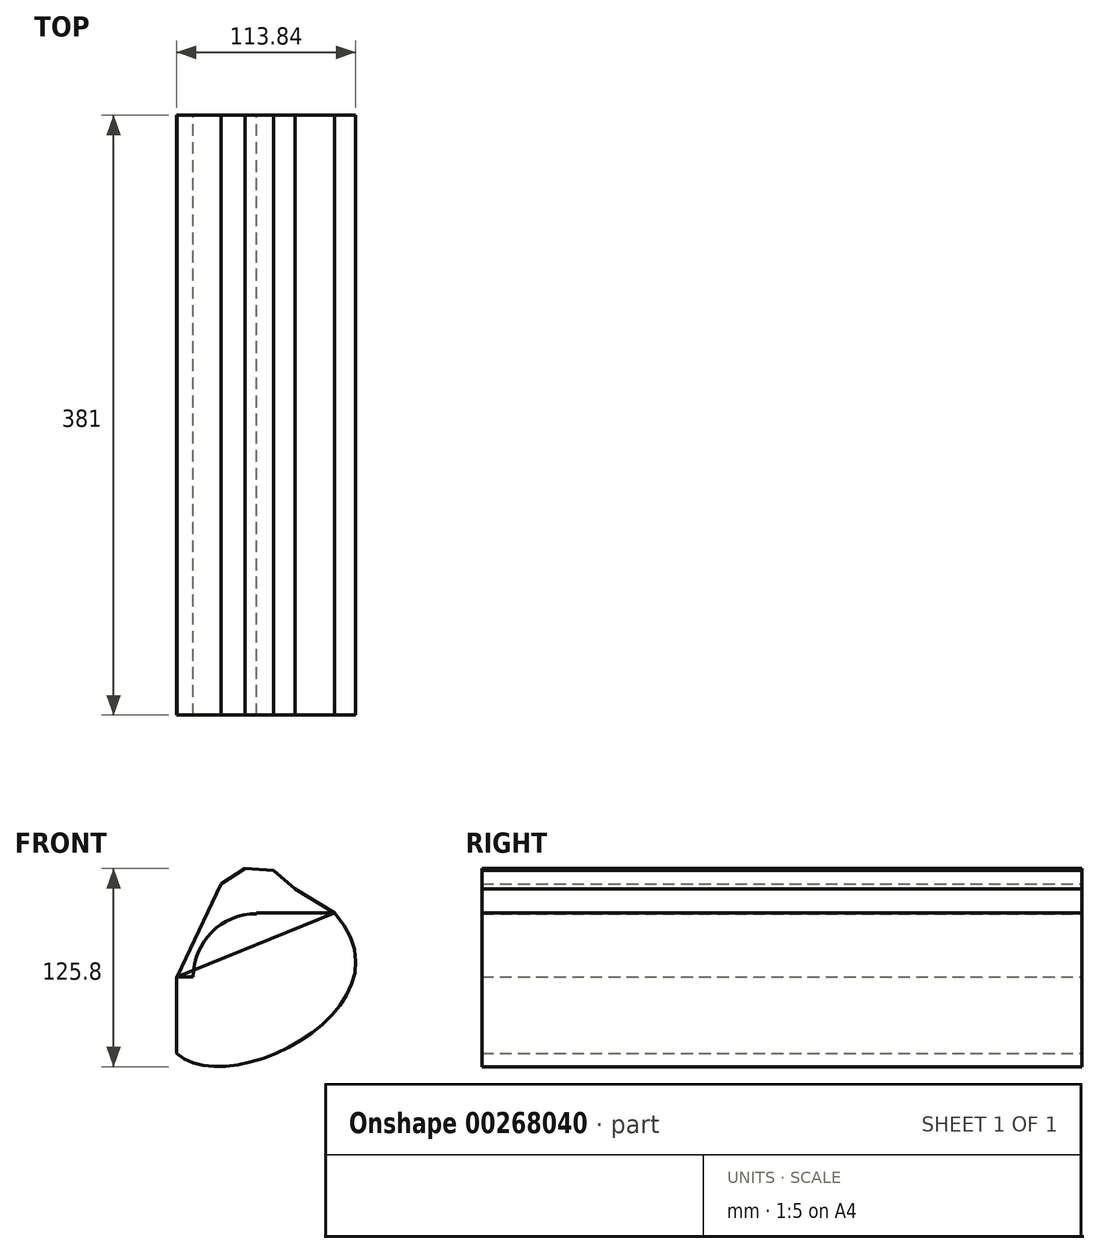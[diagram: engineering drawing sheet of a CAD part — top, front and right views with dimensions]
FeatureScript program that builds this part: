
annotation { "Feature Type Name" : "Feature", "Feature Type Description" : "" }
export const myFeature = defineFeature(function(context is Context, id is Id, definition is map)
    precondition{}
    {
        {
            var Q0;
            Q0=qCreatedBy(makeId("Front.planeOp"),FACE);
            var sketch = newSketch(context, id + "F0", { "sketchPlane" : qUnion([Q0])});
            skLineSegment(sketch, "E0.bottom", {"start": v(0, 0) * mm, "end": v(49.77, 0) * mm});
            skLineSegment(sketch, "E0.top", {"start": v(0, 40.47) * mm, "end": v(49.77, 40.47) * mm});
            skLineSegment(sketch, "E0.left", {"start": v(0, 0) * mm, "end": v(0, 40.47) * mm});
            skLineSegment(sketch, "E0.right", {"start": v(49.77, 0) * mm, "end": v(49.77, 40.47) * mm});
            skLineSegment(sketch, "E1.bottom", {"start": v(0, 0) * mm, "end": v(-50.7, 0) * mm});
            skLineSegment(sketch, "E1.top", {"start": v(0, -48.61) * mm, "end": v(-50.7, -48.61) * mm});
            skLineSegment(sketch, "E1.left", {"start": v(0, 0) * mm, "end": v(0, -48.61) * mm});
            skLineSegment(sketch, "E1.right", {"start": v(-50.7, 0) * mm, "end": v(-50.7, -48.61) * mm});
            skCircle(sketch, "E2", {"center": v(0, 0) * mm, "radius": 40.1 * mm});
            skFitSpline(sketch, "E3", {"points": [v(49.77, 40.47) * mm, v(-50.7, -48.61) * mm], "startDerivative": vector(159.79, -177.93) * mm, "endDerivative": vector(-98.38, 93.5) * mm});
            skSolve(sketch);
        }
        {
            var Q0;
            Q0=qCreatedBy(makeId("Front.planeOp"),FACE);
            var sketch = newSketch(context, id + "F1", { "sketchPlane" : qUnion([Q0])});
            skCircle(sketch, "E4.cCircle", {"center": v(0, 40.47) * mm, "radius": 27.74 * mm, "construction": true});
            skLineSegment(sketch, "E4.0", {"start": v(-7.13, 68.75) * mm, "end": v(10.85, 67.54) * mm});
            skLineSegment(sketch, "E4.1", {"start": v(10.85, 67.54) * mm, "end": v(24.7, 56) * mm});
            skLineSegment(sketch, "E4.2", {"start": v(24.7, 56) * mm, "end": v(29.1, 38.51) * mm});
            skLineSegment(sketch, "E4.3", {"start": v(29.1, 38.51) * mm, "end": v(22.4, 21.78) * mm});
            skLineSegment(sketch, "E4.4", {"start": v(22.4, 21.78) * mm, "end": v(7.13, 12.19) * mm});
            skLineSegment(sketch, "E4.5", {"start": v(7.13, 12.19) * mm, "end": v(-10.85, 13.4) * mm});
            skLineSegment(sketch, "E4.6", {"start": v(-10.85, 13.4) * mm, "end": v(-24.7, 24.95) * mm});
            skLineSegment(sketch, "E4.7", {"start": v(-24.7, 24.95) * mm, "end": v(-29.1, 42.43) * mm});
            skLineSegment(sketch, "E4.8", {"start": v(-29.1, 42.43) * mm, "end": v(-22.4, 59.16) * mm});
            skLineSegment(sketch, "E4.9", {"start": v(-22.4, 59.16) * mm, "end": v(-7.13, 68.75) * mm});
            skPoint(sketch, "E4.0.midPoint", {"position": v(1.86, 68.15) * mm});
            skLineSegment(sketch, "E5", {"start": v(-22.4, 59.16) * mm, "end": v(-50.47, 0) * mm});
            skLineSegment(sketch, "E6", {"start": v(24.7, 56) * mm, "end": v(49.77, 40.7) * mm});
            skLineSegment(sketch, "E7", {"start": v(49.77, 40.7) * mm, "end": v(-50.47, 0) * mm});
            skSolve(sketch);
        }
        {
            var Q0;
            Q0=makeQuery(id+"F1.imprint","IMPRINT",FACE,{"disambiguationData":[TD([[makeQuery(id+"F1.imprint","IMPRINT",EDGE,{"derivedFrom":sQuery(id+"F1.wireOp",EDGE,"E4.0")}),-1.0]])]});
            var Q1;
            {var subQ1=sQuery(id+"F0.wireOp",EDGE,"E0.left");var subQ3=sQuery(id+"F0.wireOp",EDGE,"E2");var subQ4=makeQuery(id+"F0.imprint","INTERSECT",VERTEX,{"derivedFrom":[subQ1,subQ3]});Q1=makeQuery(id+"F0.imprint","IMPRINT",FACE,{"disambiguationData":[TD([[makeQuery(id+"F0.imprint","IMPRINT",EDGE,{"disambiguationData":[TD([[subQ4,-1.0]])],"derivedFrom":subQ3}),1.0]])]});}
            var Q2;
            {var subQ0=sQuery(id+"F0.wireOp",EDGE,"E0.left");var subQ3=sQuery(id+"F0.wireOp",EDGE,"E2");var subQ5=makeQuery(id+"F0.imprint","INTERSECT",VERTEX,{"derivedFrom":[subQ0,subQ3]});Q2=makeQuery(id+"F0.imprint","IMPRINT",FACE,{"disambiguationData":[TD([[makeQuery(id+"F0.imprint","IMPRINT",EDGE,{"disambiguationData":[TD([[subQ5,1.0]])],"derivedFrom":subQ3}),1.0]])]});}
            var Q3;
            {var subQ4=sQuery(id+"F0.wireOp",EDGE,"E0.right");Q3=makeQuery(id+"F0.imprint","IMPRINT",FACE,{"disambiguationData":[TD([[makeQuery(id+"F0.imprint","IMPRINT",EDGE,{"derivedFrom":subQ4}),-1.0]])]});}
            var Q4;
            {var subQ0=sQuery(id+"F1.wireOp",EDGE,"E4.2");Q4=makeQuery(id+"F1.imprint","IMPRINT",FACE,{"disambiguationData":[TD([[makeQuery(id+"F1.imprint","IMPRINT",EDGE,{"derivedFrom":subQ0}),1.0]])]});}
            var Q5;
            {var subQ1=sQuery(id+"F0.wireOp",EDGE,"E1.bottom");var subQ3=sQuery(id+"F0.wireOp",EDGE,"E2");var subQ4=makeQuery(id+"F0.imprint","INTERSECT",VERTEX,{"derivedFrom":[subQ1,subQ3]});Q5=makeQuery(id+"F0.imprint","IMPRINT",FACE,{"disambiguationData":[TD([[makeQuery(id+"F0.imprint","IMPRINT",EDGE,{"disambiguationData":[TD([[subQ4,-1.0]])],"derivedFrom":subQ3}),1.0]])]});}
            var Q6;
            {var subQ2=sQuery(id+"F0.wireOp",EDGE,"E1.top");Q6=makeQuery(id+"F0.imprint","IMPRINT",FACE,{"disambiguationData":[TD([[makeQuery(id+"F0.imprint","IMPRINT",EDGE,{"derivedFrom":subQ2}),-1.0]])]});}
            var Q7;
            {var subQ1=sQuery(id+"F0.wireOp",EDGE,"E0.bottom");var subQ3=sQuery(id+"F0.wireOp",EDGE,"E2");var subQ4=makeQuery(id+"F0.imprint","INTERSECT",VERTEX,{"derivedFrom":[subQ1,subQ3]});Q7=makeQuery(id+"F0.imprint","IMPRINT",FACE,{"disambiguationData":[TD([[makeQuery(id+"F0.imprint","IMPRINT",EDGE,{"disambiguationData":[TD([[subQ4,1.0]])],"derivedFrom":subQ3}),1.0]])]});}
            var Q8;
            {var subQ6=sQuery(id+"F0.wireOp",EDGE,"E0.top");Q8=makeQuery(id+"F0.imprint","IMPRINT",FACE,{"disambiguationData":[TD([[makeQuery(id+"F0.imprint","IMPRINT",EDGE,{"derivedFrom":subQ6}),-1.0]])]});}
            var Q9;
            {var subQ1=sQuery(id+"F1.wireOp",EDGE,"E4.7");Q9=makeQuery(id+"F1.imprint","IMPRINT",FACE,{"disambiguationData":[TD([[makeQuery(id+"F1.imprint","IMPRINT",EDGE,{"derivedFrom":subQ1}),1.0]])]});}
            extrude(context, id + "F2", {"entities" : qUnion([Q0, Q1, Q2, Q3, Q4, Q5, Q6, Q7, Q8, Q9]), "depth" : 381 * mm});
        }
    });
